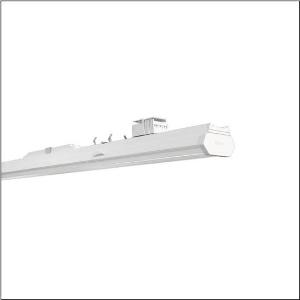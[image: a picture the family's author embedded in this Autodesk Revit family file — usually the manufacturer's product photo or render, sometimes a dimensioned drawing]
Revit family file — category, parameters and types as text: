
# Revit family: licross_11_protected_mo_51td1bdn49xg
name_source: partatom
category: Lighting Fixtures
units: mm (PartAtom-declared; Revit-internal decimal feet)

## family parameters
Cut with Voids When Loaded = No
Host = Face
Light Source = No
Part Type = Normal
Room Calculation Point = No
Round Connector Dimension = Use Diameter
Shared = No

## types (1)
- --- (1 x LED, 9370 lm, 57.1 W, 4000K)
    Apparent Load = 57 VA
    CIE Flux Codes = 54 82 95 97 100
    Color Rendering = 80
    Color Temperature = 4000K
    Default Elevation = 1800 mm
    Description = Licross 11 Protected MO, luminaire insert, of sheet steel, galvanised, coil coated, white, length: 1.500mm, width: 90mm, height: 101mm, LED rated luminous flux: 9.370lm, light colour: 840, SDCM (Standard Deviation of Colour Matching)MacAdam ≤ 2 SDCM (initial), control gear: DALI 2, with plug, 5-pole, with phase selection, mains connection: 220..240V, AC, 50/60Hz, rated input power: 57W, internal wiring halogen-free, primary optical cover: cover, of PMMA, light emission: direct distribution, primary light characteristic: symmetric, protection rating (complete): IP54, insulation class (complete): insulation class I (protective earthing), certification: CE, ENEC, VDE, UKCA, protection symbol: D if used in an environment with non-conductive dust loads with corresponding accessories, impact resistance: IK06, permissible ambient temperature for indoor applications: -25..+35°C, corresponds to IFS (International Featured Standards) requirements for safety and quality in the food industry, reducing of maximum allowable ambient temperature of 5°C with ceiling mounting, LABS conformity tested according to VDMA 24364:2018-05, The light source and the operating device comply with the requirements of the Ecodesign Regulation (EU) 2019/2020 and are replaceable in accordance with this regulation, packaging unit: 1 piece
    Height = 92 mm
    Lamp = 1 x LED
    Lamp Light Flux = 9370 lm
    Lamp Power = 57.1 W
    Lamp count = 1
    Length = 1500 mm
    Luminous efficacy = 164 lm/W
    Manufacturer = Siteco
    ModVariant = No
    Model = 51TD1BDN49XG
    Mounting Place = Ceiling
    Mounting Type = Pendant
    Number of Poles = 1
    OnlyDefault = Yes
    Power Factor = 1
    Product Name = Licross 11 Protected MO
    Product group = luminaire insert | ceiling pendant
    ProductGroupID = 901
    Protection Class = Protection class I
    Protection Degree = IP 54
    RLX_Detail_Level = 1
    RLX_Emergency_Light_Flux = 0 lm
    RLX_Emergency_Type = 0
    RLX_Emergency_Type_DB = No
    RlxData = <blob elided: 24525 chars, md5=b5a2ff31>
    Socket = socket
    Standby Power = 0 W
    System Light Flux = 9370 lm
    System Power = 57 W
    Type Comments = factory setting: luminous flux: 100 % | dim-lin: 254 | 378 mA
    Type Image = l_1256145.jpg
    URL = http://relux.com
    VarID = @adj_104365
    Voltage = 0 V
    Weight = 0.00 kg
    Width = 88 mm

## geometry (parser evidence)
native form markers: Blend x4, Sweep x10
no freeform markers — native parametric forms only
